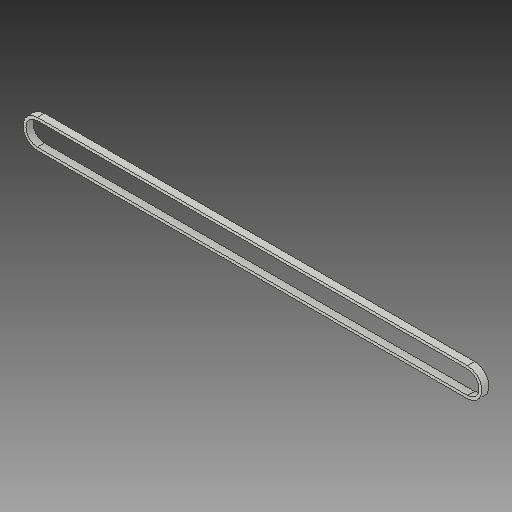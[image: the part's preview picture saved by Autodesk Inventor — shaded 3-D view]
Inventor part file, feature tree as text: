
AUTODESK INVENTOR PART (.ipt)
format: ipt  version: 2017 (Build 210142000, 142)  size: 110,080 bytes
history: native  units: in
note: dims shown in document units (in); Inventor stores cm internally (conversion verified against a paired STEP export)
features: fillet x4, extrude x1, shell x1, sketch x1
ambient origin geometry x8: Origin, YZ Plane, XZ Plane, XY Plane, X Axis, Y Axis, Z Axis, Center Point
bodies: Solid1 (feature_tree)
feature tree (7):
  extrude  "Extrusion1"  Depth=1.0in
  fillet  "Fillet1"  Radius=0.25in
  fillet  "Fillet2"  Radius=0.5in
  fillet  "Fillet3"  Radius=0.5in
  fillet  "Fillet4"  Radius=0.5in
  shell  "Shell1"  Thickness=0.5in
  sketch  "Sketch1"  dims[d0=16.0in d1=1.0in d2=0.25in d3=0.0in d4=0.5in d5=0.5in d6=0.5in d7=0.5in d8=0.1in]
